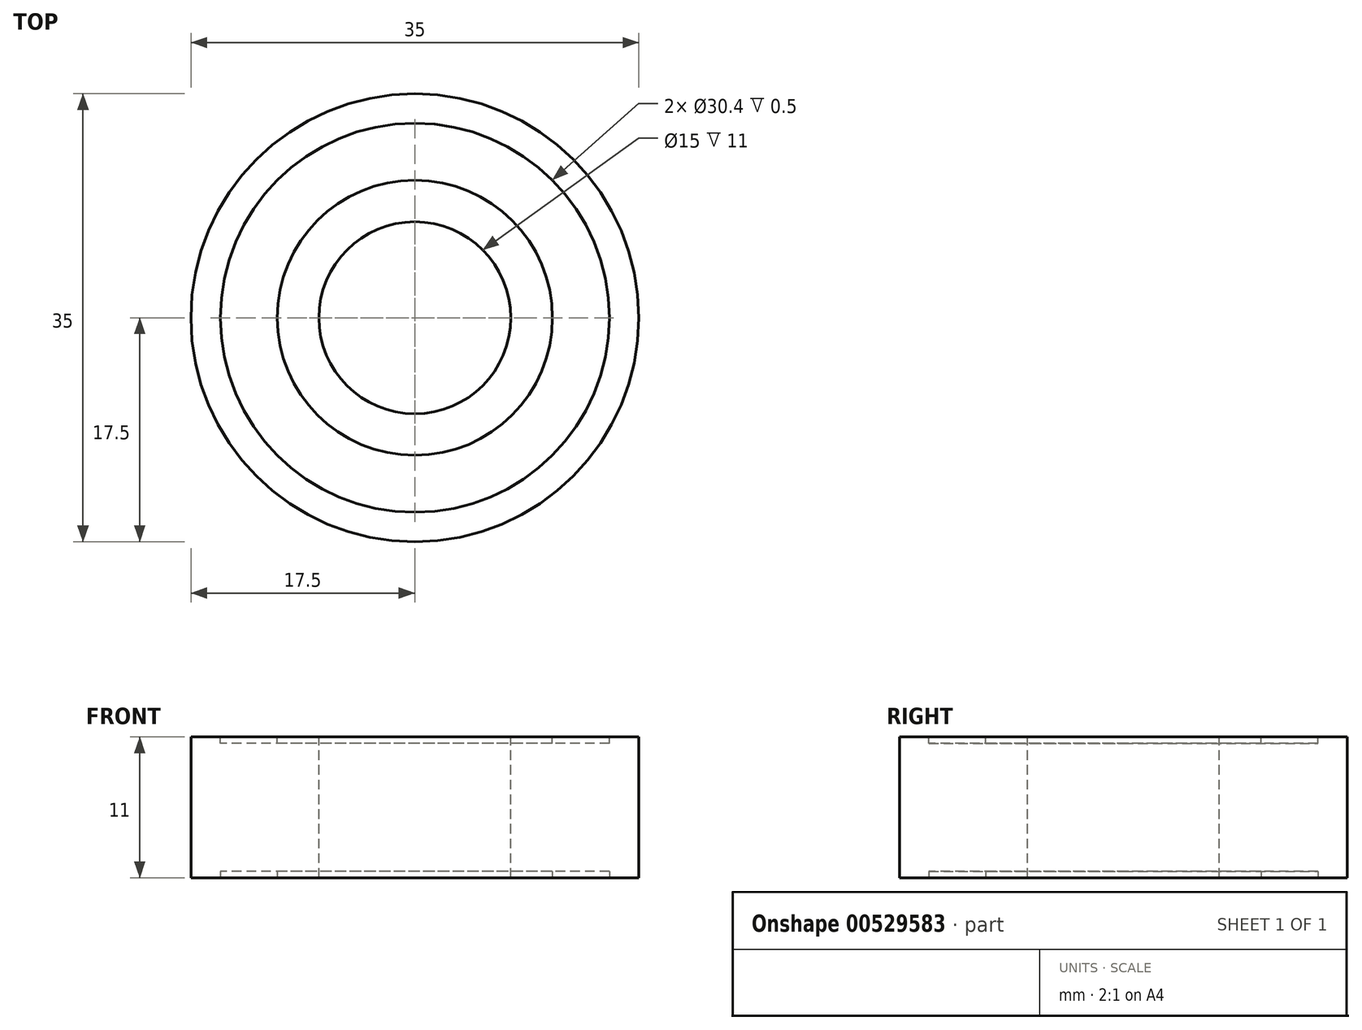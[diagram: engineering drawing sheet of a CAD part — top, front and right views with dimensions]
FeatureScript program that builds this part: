
annotation { "Feature Type Name" : "Feature", "Feature Type Description" : "" }
export const myFeature = defineFeature(function(context is Context, id is Id, definition is map)
    precondition{}
    {
        {
            var Q0;
            Q0=qCreatedBy(makeId("Top.planeOp"),FACE);
            var sketch = newSketch(context, id + "F0", { "sketchPlane" : qUnion([Q0])});
            skCircle(sketch, "E0", {"center": v(0, 0) * mm, "radius": 17.5 * mm});
            skSolve(sketch);
        }
        {
            var Q0;
            Q0 = qSketchRegion(id + "F0", true);
            extrude(context, id + "F1", {"entities" : qUnion([Q0]), "depth" : 5.5 * mm, "offsetDistance" : 25 * mm});
        }
        {
            var Q0;
            Q0=makeQuery(id+"F1.opExtrude","CAP_FACE",FACE,{"disambiguationData":[OSD([sQuery(id+"F0.wireOp",EDGE,"E0")])],"isStart":false});
            var sketch = newSketch(context, id + "F2", { "sketchPlane" : qUnion([Q0])});
            skCircle(sketch, "E1", {"center": v(0, 0) * mm, "radius": 7.5 * mm});
            skSolve(sketch);
        }
        {
            var Q0;
            Q0 = qSketchRegion(id + "F2", true);
            extrude(context, id + "F3", {"entities" : qUnion([Q0]), "operationType" : NewBodyOperationType.REMOVE, "oppositeDirection" : true, "depth" : 25 * mm, "offsetDistance" : 25 * mm});
        }
        {
            var Q0;
            Q0=makeQuery(id+"F1.opExtrude","CAP_FACE",FACE,{"disambiguationData":[OSD([sQuery(id+"F0.wireOp",EDGE,"E0")])],"isStart":false});
            var sketch = newSketch(context, id + "F4", { "sketchPlane" : qUnion([Q0])});
            skCircle(sketch, "E2", {"center": v(0, 0) * mm, "radius": 10.75 * mm});
            skCircle(sketch, "E3", {"center": v(0, 0) * mm, "radius": 15.2 * mm});
            skSolve(sketch);
        }
        {
            var Q0;
            Q0=makeQuery(id+"F4.imprint","IMPRINT",FACE,{"disambiguationData":[TD([[makeQuery(id+"F4.imprint","IMPRINT",EDGE,{"derivedFrom":sQuery(id+"F4.wireOp",EDGE,"E2")}),-1.0]])]});
            extrude(context, id + "F5", {"entities" : qUnion([Q0]), "operationType" : NewBodyOperationType.REMOVE, "oppositeDirection" : true, "depth" : .5 * mm, "offsetDistance" : 25 * mm});
        }
        {
            var Q0;
            Q0=makeQuery(id+"F1.opExtrude","SWEPT_BODY",BODY,{"disambiguationData":[OSD([sQuery(id+"F0.wireOp",EDGE,"E0")])]});
            var Q1;
            Q1=qCreatedBy(makeId("Top.planeOp"),FACE);
            mirror(context, id + "F6", {"operationType" : NewBodyOperationType.ADD, "entities" : qUnion([Q0]), "mirrorPlane" : qUnion([Q1])});
        }
    });
